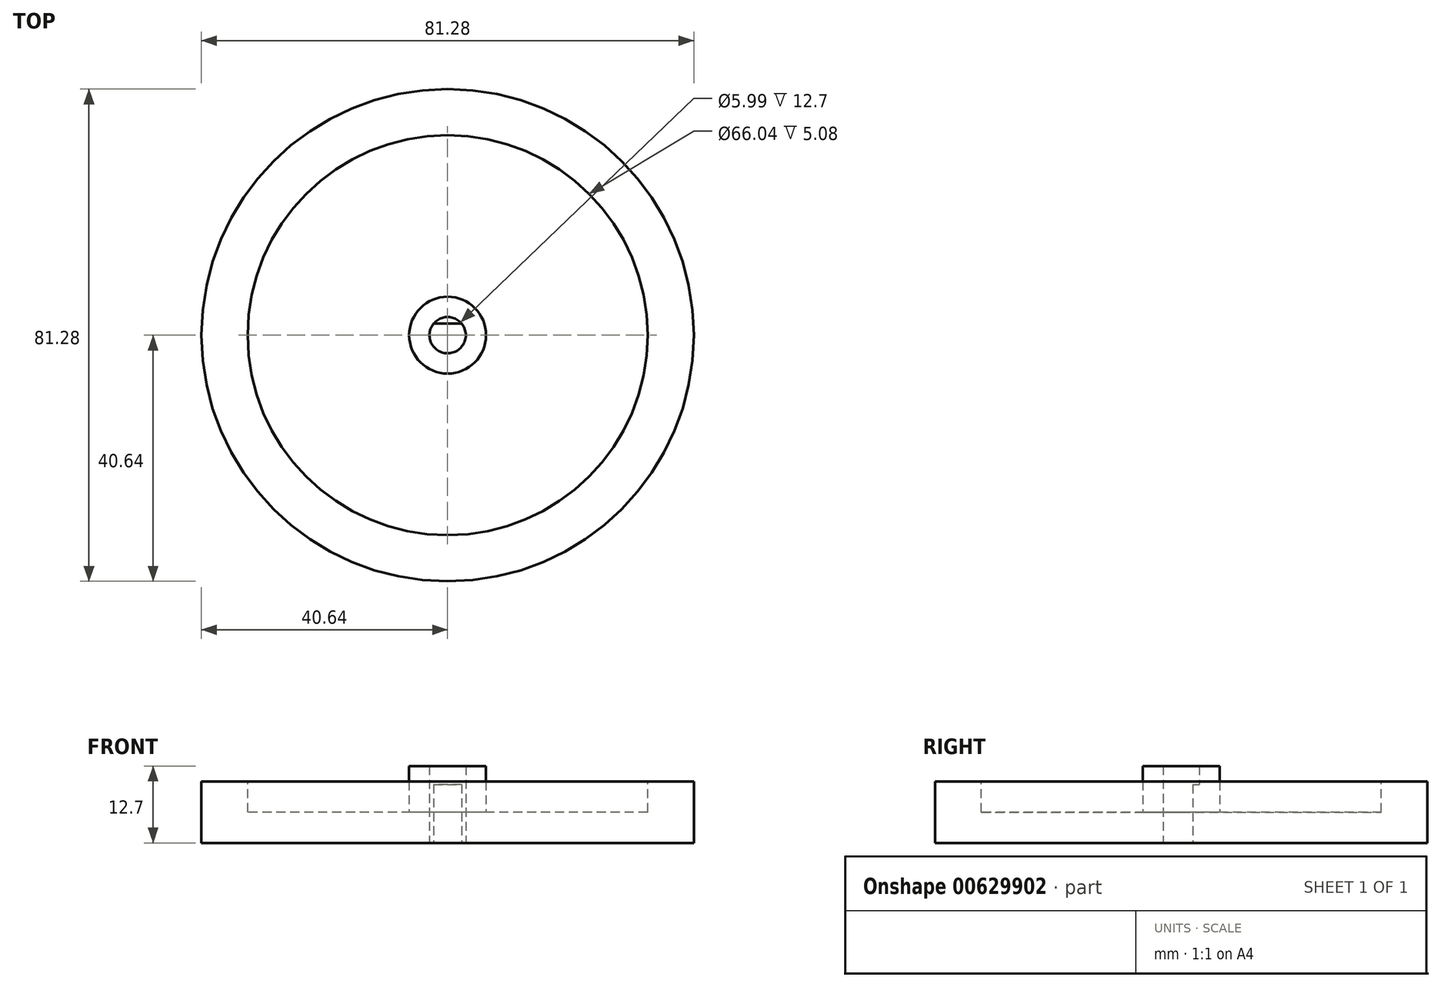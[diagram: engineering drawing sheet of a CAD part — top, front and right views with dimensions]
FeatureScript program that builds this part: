
annotation { "Feature Type Name" : "Feature", "Feature Type Description" : "" }
export const myFeature = defineFeature(function(context is Context, id is Id, definition is map)
    precondition{}
    {
        {
            var Q0;
            Q0=qCreatedBy(makeId("Top.planeOp"),FACE);
            var sketch = newSketch(context, id + "F0", { "sketchPlane" : qUnion([Q0])});
            skCircle(sketch, "E0", {"center": v(0, 0) * mm, "radius": 40.64 * mm});
            skSolve(sketch);
        }
        {
            var Q0;
            Q0=makeQuery(id+"F0.imprint","IMPRINT",FACE,{"disambiguationData":[TD([[makeQuery(id+"F0.imprint","IMPRINT",EDGE,{"derivedFrom":sQuery(id+"F0.wireOp",EDGE,"E0")}),1.0]])]});
            extrude(context, id + "F1", {"entities" : qUnion([Q0]), "depth" : 10.16 * mm, "offsetDistance" : 25.4 * mm});
        }
        {
            var Q0;
            Q0=makeQuery(id+"F1.opExtrude","CAP_FACE",FACE,{"disambiguationData":[OSD([sQuery(id+"F0.wireOp",EDGE,"E0")])],"isStart":false});
            var sketch = newSketch(context, id + "F2", { "sketchPlane" : qUnion([Q0])});
            skCircle(sketch, "E1", {"center": v(0, 0) * mm, "radius": 33.02 * mm});
            skSolve(sketch);
        }
        {
            var Q0;
            Q0=makeQuery(id+"F2.imprint","IMPRINT",FACE,{"disambiguationData":[TD([[makeQuery(id+"F2.imprint","IMPRINT",EDGE,{"derivedFrom":sQuery(id+"F2.wireOp",EDGE,"E1")}),1.0]])]});
            extrude(context, id + "F3", {"entities" : qUnion([Q0]), "operationType" : NewBodyOperationType.REMOVE, "oppositeDirection" : true, "depth" : 5.08 * mm, "offsetDistance" : 25.4 * mm});
        }
        {
            var Q0;
            Q0=makeQuery(id+"F1.opExtrude","CAP_FACE",FACE,{"disambiguationData":[OSD([sQuery(id+"F0.wireOp",EDGE,"E0")])],"isStart":true});
            var sketch = newSketch(context, id + "F4", { "sketchPlane" : qUnion([Q0])});
            skCircle(sketch, "E2", {"center": v(0, 0) * mm, "radius": 3 * mm});
            skLineSegment(sketch, "E3.bottom", {"start": v(-3.8, -4.44) * mm, "end": v(3.81, -4.44) * mm});
            skLineSegment(sketch, "E3.top", {"start": v(-3.8, -1.9) * mm, "end": v(3.81, -1.9) * mm});
            skLineSegment(sketch, "E3.left", {"start": v(-3.8, -4.44) * mm, "end": v(-3.8, -1.9) * mm});
            skLineSegment(sketch, "E3.right", {"start": v(3.81, -4.44) * mm, "end": v(3.81, -1.9) * mm});
            skSolve(sketch);
        }
        {
            var Q0;
            Q0=makeQuery(id+"F4.imprint","IMPRINT",FACE,{"disambiguationData":[TD([[makeQuery(id+"F4.imprint","IMPRINT",EDGE,{"derivedFrom":sQuery(id+"F4.wireOp",EDGE,"E2")}),1.0]])]});
            extrude(context, id + "F5", {"entities" : qUnion([Q0]), "operationType" : NewBodyOperationType.REMOVE, "oppositeDirection" : true, "depth" : 10.16 * mm, "offsetDistance" : 25.4 * mm});
        }
        {
            var Q0;
            Q0=makeQuery(id+"F3.boolean.opBoolean","COPY",FACE,{"derivedFrom":makeQuery(id+"F3.opExtrude","CAP_FACE",FACE,{"disambiguationData":[OSD([sQuery(id+"F2.wireOp",EDGE,"E1")])],"isStart":false})});
            var sketch = newSketch(context, id + "F6", { "sketchPlane" : qUnion([Q0])});
            skCircle(sketch, "E4", {"center": v(0, 0) * mm, "radius": 6.35 * mm});
            skSolve(sketch);
        }
        {
            var Q0;
            Q0=makeQuery(id+"F6.imprint","IMPRINT",FACE,{"disambiguationData":[TD([[makeQuery(id+"F6.imprint","IMPRINT",EDGE,{"derivedFrom":sQuery(id+"F6.wireOp",EDGE,"E4")}),1.0]])]});
            extrude(context, id + "F7", {"entities" : qUnion([Q0]), "operationType" : NewBodyOperationType.ADD, "depth" : 7.62 * mm, "offsetDistance" : 25.4 * mm, "hasSecondDirection" : true, "secondDirectionOppositeDirection" : true, "secondDirectionDepth" : 0.01 * mm});
        }
        {
            var Q0;
            Q0=qCreatedBy(makeId("Top.planeOp"),FACE);
            var sketch = newSketch(context, id + "F8", { "sketchPlane" : qUnion([Q0])});
            skLineSegment(sketch, "E5.bottom", {"start": v(-3.81, 4.45) * mm, "end": v(3.8, 4.45) * mm});
            skLineSegment(sketch, "E5.top", {"start": v(-3.81, 1.9) * mm, "end": v(3.8, 1.9) * mm});
            skLineSegment(sketch, "E5.left", {"start": v(-3.81, 4.45) * mm, "end": v(-3.81, 1.9) * mm});
            skLineSegment(sketch, "E5.right", {"start": v(3.8, 4.45) * mm, "end": v(3.8, 1.9) * mm});
            skSolve(sketch);
        }
        {
            var Q0;
            Q0=makeQuery(id+"F8.imprint","IMPRINT",FACE,{"disambiguationData":[TD([[makeQuery(id+"F8.imprint","IMPRINT",EDGE,{"derivedFrom":sQuery(id+"F8.wireOp",EDGE,"E5.bottom")}),-1.0]])]});
            extrude(context, id + "F9", {"entities" : qUnion([Q0]), "operationType" : NewBodyOperationType.ADD, "depth" : 9.65 * mm, "offsetDistance" : 25.4 * mm});
        }
    });
